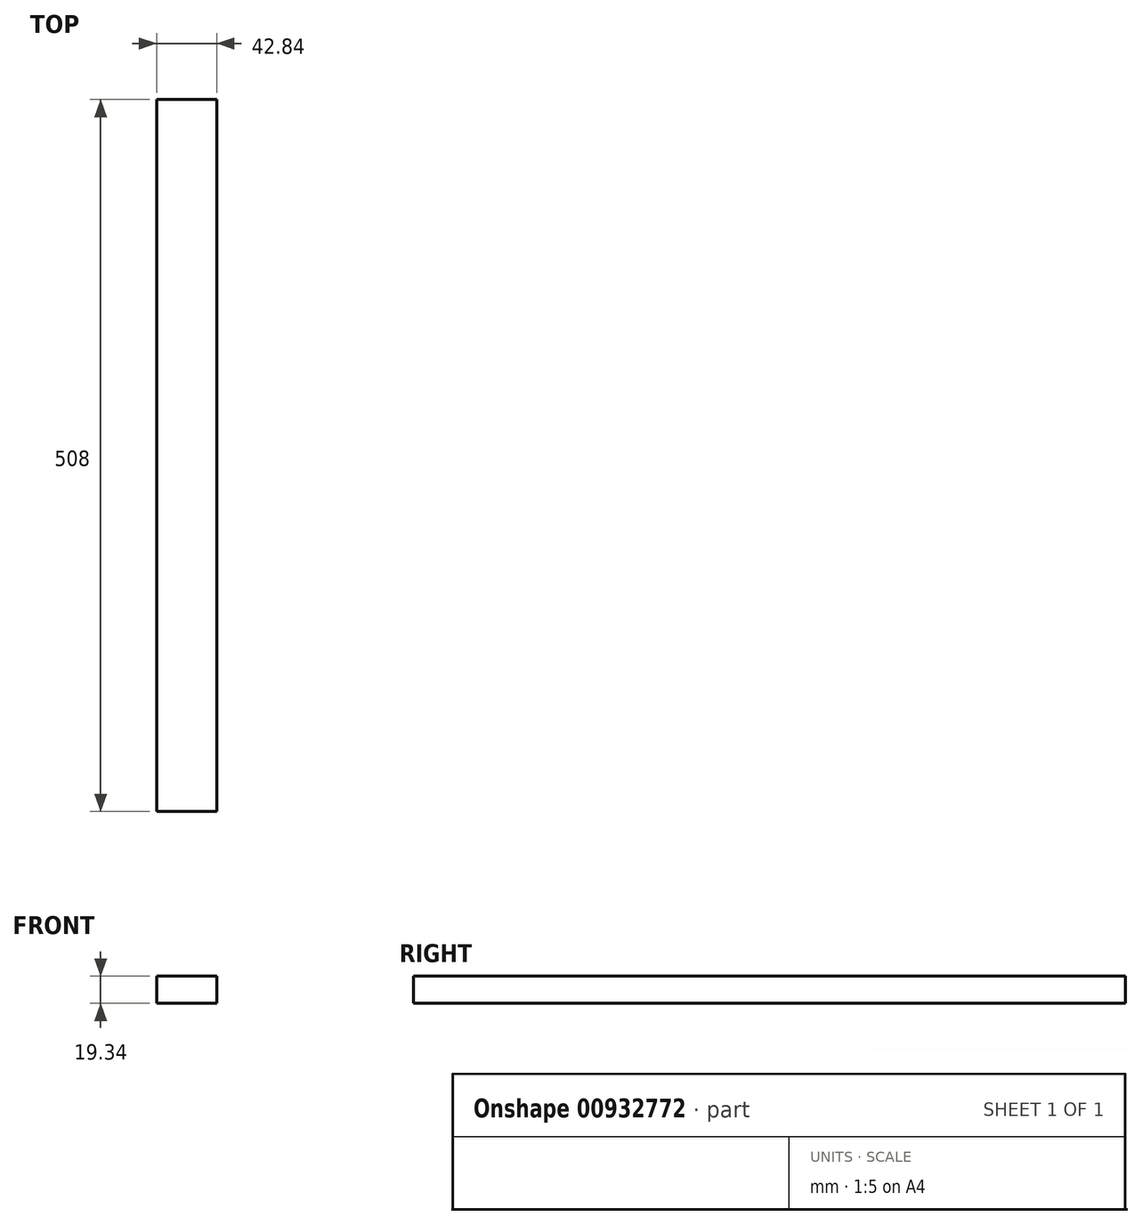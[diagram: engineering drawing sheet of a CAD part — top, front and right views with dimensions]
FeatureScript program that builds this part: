
annotation { "Feature Type Name" : "Feature", "Feature Type Description" : "" }
export const myFeature = defineFeature(function(context is Context, id is Id, definition is map)
    precondition{}
    {
        {
            var Q0;
            Q0=qCreatedBy(makeId("Front.planeOp"),FACE);
            var sketch = newSketch(context, id + "F0", { "sketchPlane" : qUnion([Q0])});
            skLineSegment(sketch, "E0.bottom", {"start": v(-89.77, 35.55) * mm, "end": v(-46.93, 35.55) * mm});
            skLineSegment(sketch, "E0.top", {"start": v(-89.77, 16.21) * mm, "end": v(-46.93, 16.21) * mm});
            skLineSegment(sketch, "E0.left", {"start": v(-89.77, 35.55) * mm, "end": v(-89.77, 16.21) * mm});
            skLineSegment(sketch, "E0.right", {"start": v(-46.93, 35.55) * mm, "end": v(-46.93, 16.21) * mm});
            skSolve(sketch);
        }
        {
            var Q0;
            Q0 = qSketchRegion(id + "F0", true);
            extrude(context, id + "F1", {"entities" : qUnion([Q0]), "oppositeDirection" : true, "depth" : 508 * mm, "offsetDistance" : 25.4 * mm});
        }
    });
